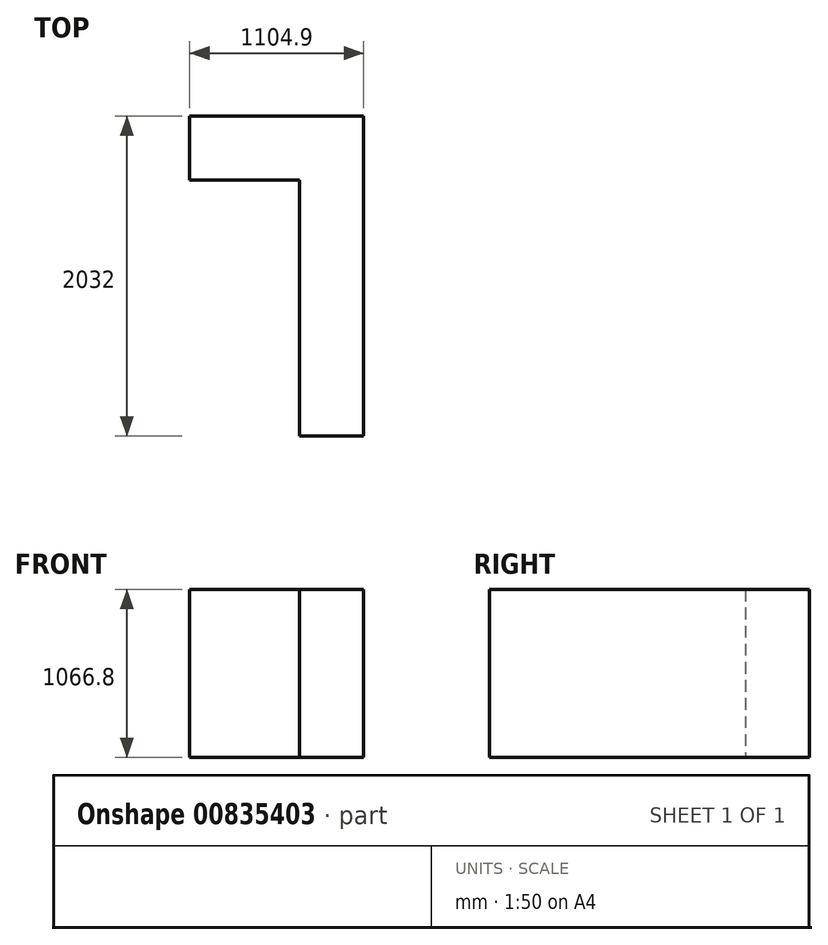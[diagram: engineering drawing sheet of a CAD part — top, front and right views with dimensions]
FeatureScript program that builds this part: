
annotation { "Feature Type Name" : "Feature", "Feature Type Description" : "" }
export const myFeature = defineFeature(function(context is Context, id is Id, definition is map)
    precondition{}
    {
        {
            var Q0;
            Q0=qCreatedBy(makeId("Top.planeOp"),FACE);
            var sketch = newSketch(context, id + "F0", { "sketchPlane" : qUnion([Q0])});
            skLineSegment(sketch, "E0.bottom", {"start": v(87.54, -303.48) * mm, "end": v(-1017.36, -303.48) * mm});
            skLineSegment(sketch, "E0.top", {"start": v(87.54, 1728.52) * mm, "end": v(-1017.36, 1728.52) * mm});
            skLineSegment(sketch, "E0.left", {"start": v(87.54, -303.48) * mm, "end": v(87.54, 1728.52) * mm});
            skLineSegment(sketch, "E0.right", {"start": v(-1017.36, -303.48) * mm, "end": v(-1017.36, 1728.52) * mm});
            skLineSegment(sketch, "E1.bottom", {"start": v(-1017.36, -303.48) * mm, "end": v(-318.86, -303.48) * mm});
            skLineSegment(sketch, "E1.top", {"start": v(-1017.36, 1322.12) * mm, "end": v(-318.86, 1322.12) * mm});
            skLineSegment(sketch, "E1.left", {"start": v(-1017.36, -303.48) * mm, "end": v(-1017.36, 1322.12) * mm});
            skLineSegment(sketch, "E1.right", {"start": v(-318.86, -303.48) * mm, "end": v(-318.86, 1322.12) * mm});
            skSolve(sketch);
        }
        {
            var Q0;
            {var subQ1=sQuery(id+"F0.wireOp",EDGE,"E0.top");Q0=makeQuery(id+"F0.imprint","IMPRINT",FACE,{"disambiguationData":[TD([[makeQuery(id+"F0.imprint","IMPRINT",EDGE,{"derivedFrom":subQ1}),1.0]])]});}
            extrude(context, id + "F1", {"entities" : qUnion([Q0]), "depth" : 1066.8 * mm, "offsetDistance" : 25.4 * mm});
        }
    });
